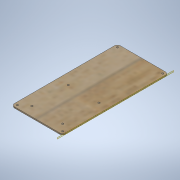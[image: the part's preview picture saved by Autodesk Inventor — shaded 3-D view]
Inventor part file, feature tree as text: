
AUTODESK INVENTOR PART (.ipt)
format: ipt  version: 2020.3 (Build 243373000, 373)  size: 150,528 bytes
history: native  units: mm
features: sketch x3, other x2, hole x2, extrude x1, fillet x1
ambient origin geometry x8: Origin, YZ Plane, XZ Plane, XY Plane, X Axis, Y Axis, Z Axis, Center Point
bodies: Body1 (feature_tree)
feature tree (9):
  other  "ソリッド1"
  extrude  "押し出し1"  Depth=169.0mm
  fillet  "フィレット1"  Radius=2.0mm
  hole  "穴2"  [1 undecoded]
  hole  "穴3"  [1 undecoded]
  other  "作業平面1"
  sketch  "スケッチ1"
  sketch  "スケッチ3"
  sketch  "スケッチ4"
note: 2 required parameter values undecoded (feature->parameter linkage not recoverable at this tier; creation-order binding heuristic only, values carry confidence <= 0.55)
